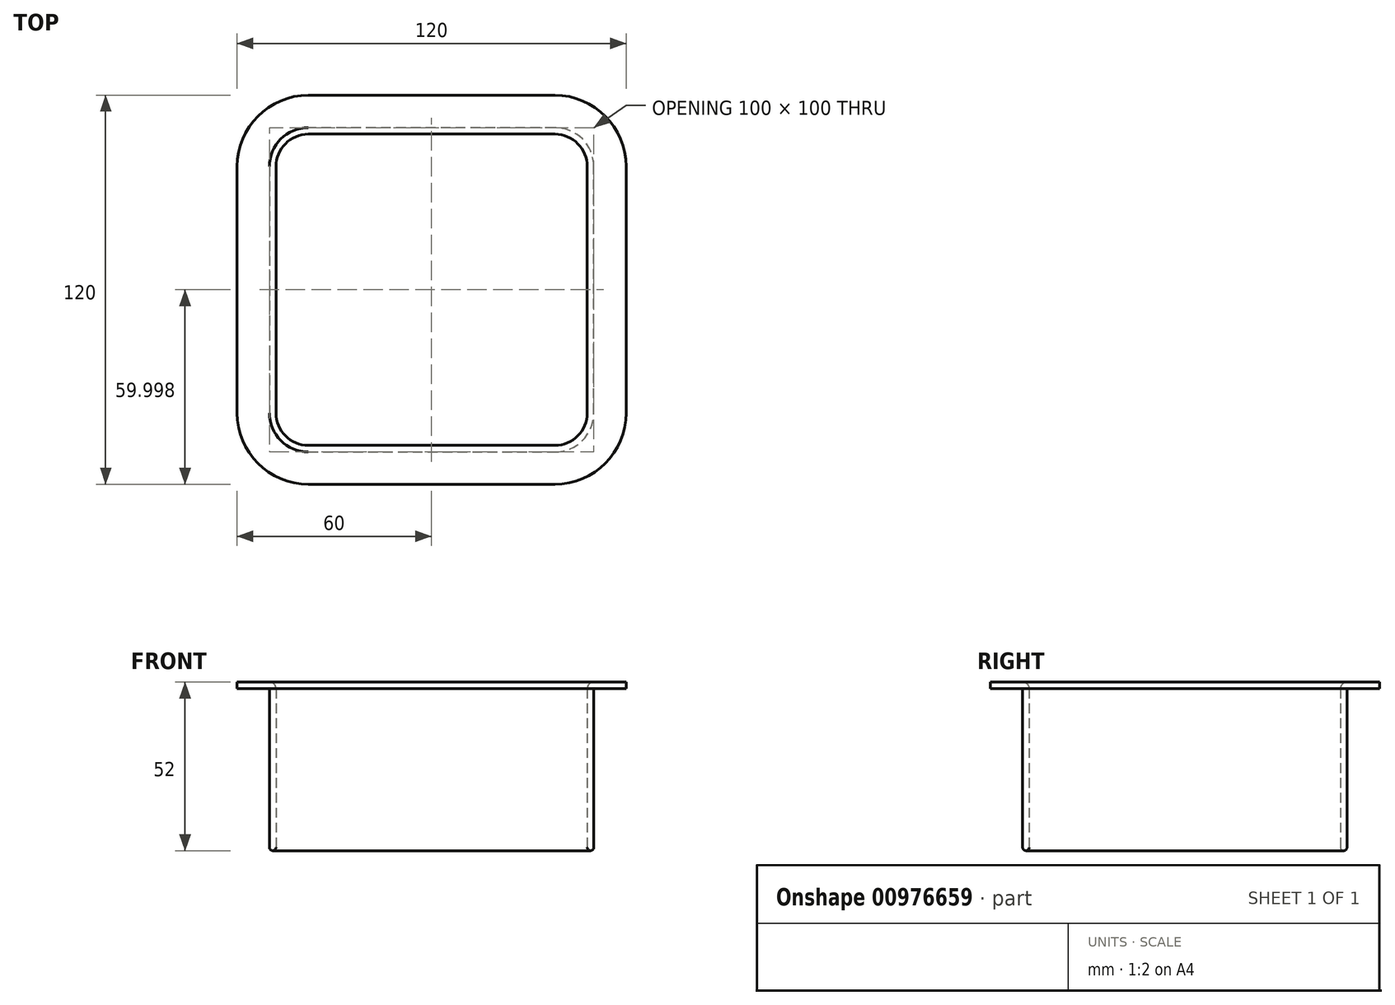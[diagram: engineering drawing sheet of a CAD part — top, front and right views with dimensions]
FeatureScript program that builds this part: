
annotation { "Feature Type Name" : "Feature", "Feature Type Description" : "" }
export const myFeature = defineFeature(function(context is Context, id is Id, definition is map)
    precondition{}
    {
        {
            var Q0;
            Q0=qCreatedBy(makeId("Top.planeOp"),FACE);
            var sketch = newSketch(context, id + "F0", { "sketchPlane" : qUnion([Q0])});
            skLineSegment(sketch, "E0", {"start": v(-45.3, 54.48) * mm, "end": v(30.7, 54.48) * mm});
            skLineSegment(sketch, "E1", {"start": v(40.7, 44.48) * mm, "end": v(40.7, -31.52) * mm});
            skLineSegment(sketch, "E2", {"start": v(30.7, -41.52) * mm, "end": v(-45.3, -41.52) * mm});
            skLineSegment(sketch, "E3", {"start": v(-55.3, -31.52) * mm, "end": v(-55.3, 44.48) * mm});
            skPoint(sketch, "E4.visualSharp", {"position": v(-55.3, 54.48) * mm});
            skArc(sketch, "E4.filletArc", {"start": v(-45.3, 54.48) * mm, "mid": v(-52.38, 51.55) * mm, "end": v(-55.3, 44.48) * mm});
            skPoint(sketch, "E5.visualSharp", {"position": v(40.7, 54.48) * mm});
            skArc(sketch, "E5.filletArc", {"start": v(40.7, 44.48) * mm, "mid": v(37.76, 51.55) * mm, "end": v(30.7, 54.48) * mm});
            skPoint(sketch, "E6.visualSharp", {"position": v(40.7, -41.52) * mm});
            skArc(sketch, "E6.filletArc", {"start": v(30.7, -41.52) * mm, "mid": v(37.76, -38.6) * mm, "end": v(40.7, -31.52) * mm});
            skPoint(sketch, "E7.visualSharp", {"position": v(-55.3, -41.52) * mm});
            skArc(sketch, "E7.filletArc", {"start": v(-55.3, -31.52) * mm, "mid": v(-52.38, -38.6) * mm, "end": v(-45.3, -41.52) * mm});
            skLineSegment(sketch, "E8.0", {"start": v(-67.3, -31.52) * mm, "end": v(-67.3, 44.48) * mm});
            skArc(sketch, "E8.1", {"start": v(-45.3, 66.48) * mm, "mid": v(-60.87, 60.03) * mm, "end": v(-67.3, 44.48) * mm});
            skArc(sketch, "E8.2", {"start": v(-67.3, -31.52) * mm, "mid": v(-60.87, -47.08) * mm, "end": v(-45.3, -53.52) * mm});
            skLineSegment(sketch, "E8.3", {"start": v(-45.3, 66.48) * mm, "end": v(30.7, 66.48) * mm});
            skLineSegment(sketch, "E8.4", {"start": v(30.7, -53.52) * mm, "end": v(-45.3, -53.52) * mm});
            skArc(sketch, "E8.5", {"start": v(30.7, -53.52) * mm, "mid": v(46.25, -47.08) * mm, "end": v(52.7, -31.52) * mm});
            skLineSegment(sketch, "E8.6", {"start": v(52.7, 44.48) * mm, "end": v(52.7, -31.52) * mm});
            skArc(sketch, "E8.7", {"start": v(52.7, 44.48) * mm, "mid": v(46.25, 60.03) * mm, "end": v(30.7, 66.48) * mm});
            skSolve(sketch);
        }
        {
            var Q0;
            Q0=makeQuery(id+"F0.imprint","IMPRINT",FACE,{"disambiguationData":[TD([[makeQuery(id+"F0.imprint","IMPRINT",EDGE,{"derivedFrom":sQuery(id+"F0.wireOp",EDGE,"E0")}),1.0]])]});
            extrude(context, id + "F1", {"entities" : qUnion([Q0]), "depth" : 2 * mm, "offsetDistance" : 25 * mm});
        }
        {
            var Q0;
            Q0=qCreatedBy(makeId("Top.planeOp"),FACE);
            var sketch = newSketch(context, id + "F2", { "sketchPlane" : qUnion([Q0])});
            skArc(sketch, "E9.0", {"start": v(30.7, -43.52) * mm, "mid": v(39.18, -40) * mm, "end": v(42.7, -31.52) * mm});
            skLineSegment(sketch, "E9.1", {"start": v(-45.3, -43.52) * mm, "end": v(30.7, -43.52) * mm});
            skLineSegment(sketch, "E9.2", {"start": v(42.7, -31.52) * mm, "end": v(42.7, 44.48) * mm});
            skArc(sketch, "E9.3", {"start": v(-57.3, -31.52) * mm, "mid": v(-53.8, -40) * mm, "end": v(-45.3, -43.52) * mm});
            skArc(sketch, "E9.4", {"start": v(42.7, 44.48) * mm, "mid": v(39.18, 52.96) * mm, "end": v(30.7, 56.48) * mm});
            skLineSegment(sketch, "E9.5", {"start": v(30.7, 56.48) * mm, "end": v(-45.3, 56.48) * mm});
            skArc(sketch, "E9.6", {"start": v(-45.3, 56.48) * mm, "mid": v(-53.8, 52.96) * mm, "end": v(-57.3, 44.48) * mm});
            skLineSegment(sketch, "E9.7", {"start": v(-57.3, 44.48) * mm, "end": v(-57.3, -31.52) * mm});
            skLineSegment(sketch, "E10.0", {"start": v(30.7, 54.48) * mm, "end": v(-45.3, 54.48) * mm});
            skArc(sketch, "E10.1", {"start": v(40.7, 44.48) * mm, "mid": v(37.76, 51.55) * mm, "end": v(30.7, 54.48) * mm});
            skArc(sketch, "E10.2", {"start": v(-45.3, 54.48) * mm, "mid": v(-52.38, 51.55) * mm, "end": v(-55.3, 44.48) * mm});
            skLineSegment(sketch, "E10.3", {"start": v(40.7, -31.52) * mm, "end": v(40.7, 44.48) * mm});
            skLineSegment(sketch, "E10.4", {"start": v(-55.3, 44.48) * mm, "end": v(-55.3, -31.52) * mm});
            skArc(sketch, "E10.5", {"start": v(-55.3, -31.52) * mm, "mid": v(-52.38, -38.6) * mm, "end": v(-45.3, -41.52) * mm});
            skLineSegment(sketch, "E10.6", {"start": v(-45.3, -41.52) * mm, "end": v(30.7, -41.52) * mm});
            skArc(sketch, "E10.7", {"start": v(30.7, -41.52) * mm, "mid": v(37.76, -38.6) * mm, "end": v(40.7, -31.52) * mm});
            skSolve(sketch);
        }
        {
            var Q0;
            Q0=makeQuery(id+"F2.imprint","IMPRINT",FACE,{"disambiguationData":[TD([[makeQuery(id+"F2.imprint","IMPRINT",EDGE,{"derivedFrom":sQuery(id+"F2.wireOp",EDGE,"E9.0")}),1.0]])]});
            extrude(context, id + "F3", {"entities" : qUnion([Q0]), "operationType" : NewBodyOperationType.ADD, "oppositeDirection" : true, "depth" : 50 * mm, "offsetDistance" : 25 * mm});
        }
        {
            var Q0;
            Q0=makeQuery(id+"F3.opExtrude","CAP_EDGE",EDGE,{"disambiguationData":[OSD([sQuery(id+"F2.wireOp",EDGE,"E10.4")])],"isStart":false});
            var Q1;
            Q1=makeQuery(id+"F3.opExtrude","CAP_EDGE",EDGE,{"disambiguationData":[OSD([sQuery(id+"F2.wireOp",EDGE,"E9.7")])],"isStart":false});
            fillet(context, id + "F4", {"entities" : qUnion([Q0, Q1]), "radius" : 1 * mm, "tangentPropagation" : true, "allowEdgeOverflow" : false});
        }
        {
            var Q0;
            Q0=makeQuery(id+"F1.opExtrude","CAP_EDGE",EDGE,{"disambiguationData":[OSD([sQuery(id+"F0.wireOp",EDGE,"E0")])],"isStart":false});
            fillet(context, id + "F5", {"entities" : qUnion([Q0]), "radius" : 2 * mm, "tangentPropagation" : true, "allowEdgeOverflow" : false});
        }
    });
